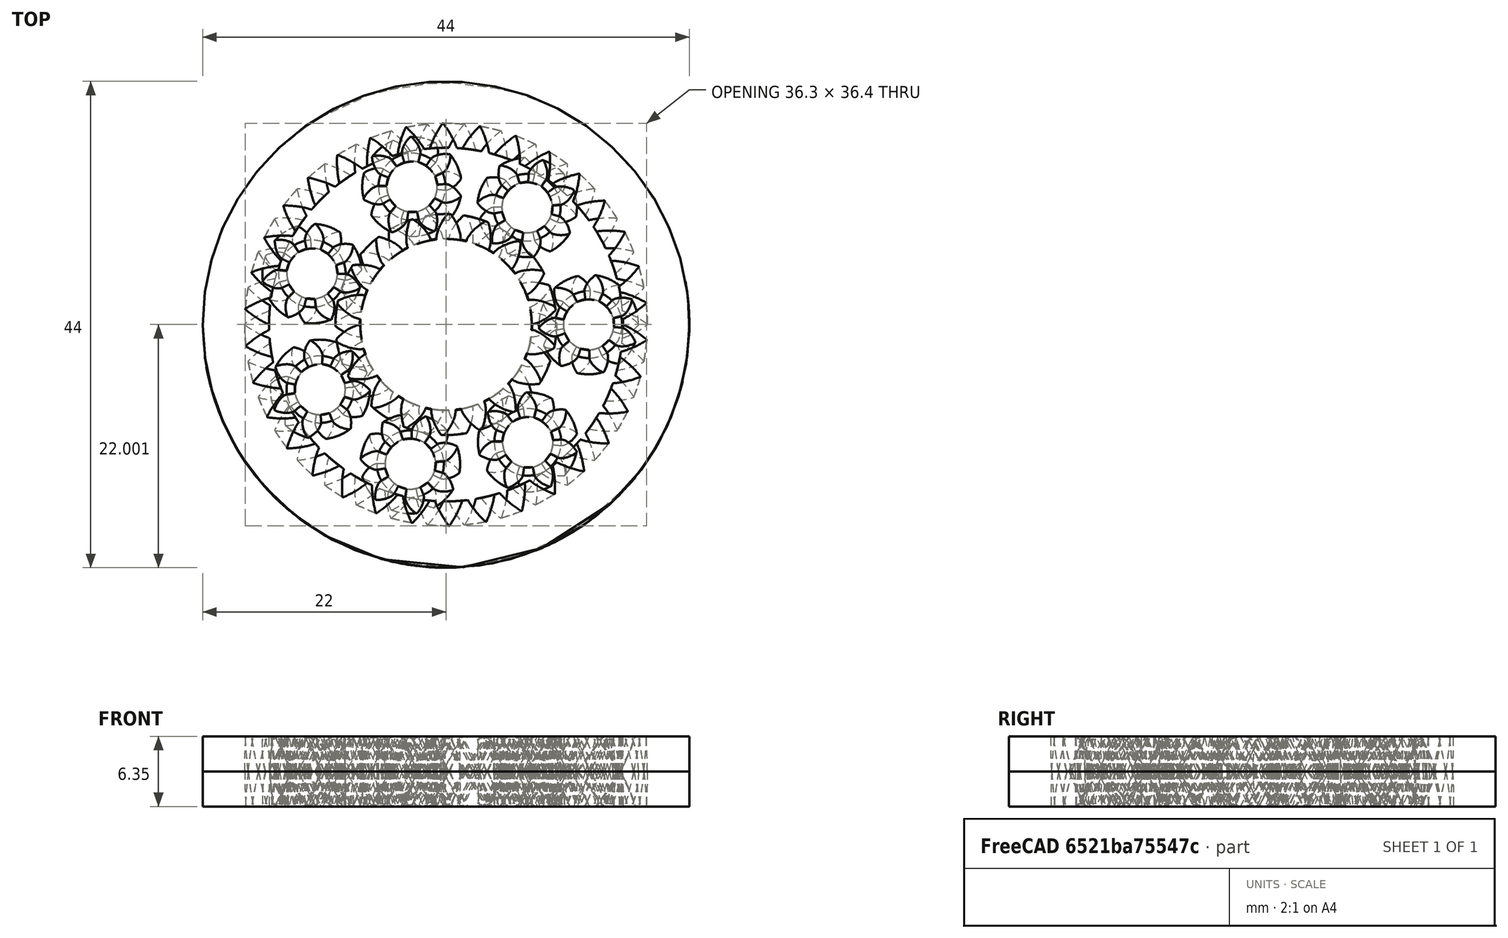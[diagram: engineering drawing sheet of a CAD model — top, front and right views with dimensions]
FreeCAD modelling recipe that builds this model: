
FCSTD DOCUMENT  (FreeCAD 0.20R29410 (Git))
Label: bearing
License: All rights reserved
LicenseURL: http://en.wikipedia.org/wiki/All_rights_reserved
objects: PartDesign::FeatureBase×8, PartDesign::Body×8, Part::FeaturePython×3
note: 19 computed .brp shape members not serialized (recipe doc carries the construction recipe); baked Part::Feature solids carry a one-line shape summary decoded from their .brp

FEATURE [Part::FeaturePython] InternalInvoluteGear  # WARN: FeaturePython — macro-defined, semantics opaque (R4)
  AttacherType = Attacher::AttachEngine3D
  angular_backlash = 0
  backlash = 0
  beta = 30
  clearance = 0.2
  da = 32
  df = 36.4
  double_helix = true
  dw = 34
  head = 0
  head_fillet = 0
  height = 6.35
  module = 1
  numpoints = 6
  outside_diameter = 44
  pressure_angle = 30
  properties_from_tool = false
  reversed_backlash = false
  root_fillet = 0
  shift = 0
  simple = false
  teeth = 34
  thickness = 5
  transverse_pitch = 3.14159
  version = 0.0.4
  expr: angular_backlash = backlash / dw * 360° / pi
  expr: dw = teeth * module
FEATURE [Part::FeaturePython] InvoluteGear  # WARN: FeaturePython — macro-defined, semantics opaque (R4)
  AttacherType = Attacher::AttachEngine3D
  Placement = pos=(12.9,0,0) rot=(0,0,1;0rad)
  angular_backlash = 0
  backlash = 0
  beta = 30
  clearance = 0.2
  da = 9
  df = 4.6
  double_helix = true
  dw = 7
  head = 0
  head_fillet = 0
  height = 6.35
  module = 1
  numpoints = 6
  pressure_angle = 30
  properties_from_tool = false
  reversed_backlash = false
  root_fillet = 0
  shift = 0
  simple = false
  teeth = 7
  transverse_pitch = 3.14159
  undercut = false
  version = 0.0.4
  expr: angular_backlash = backlash / dw * 360° / pi
  expr: dw = teeth * module
FEATURE [Part::FeaturePython] InvoluteGear001  # WARN: FeaturePython — macro-defined, semantics opaque (R4)
  AttacherType = Attacher::AttachEngine3D
  angular_backlash = 0
  backlash = 0
  beta = -30
  clearance = 0.25
  da = 20
  df = 15.5
  double_helix = true
  dw = 18
  head = 0
  head_fillet = 0
  height = 6.35
  module = 1
  numpoints = 6
  pressure_angle = 30
  properties_from_tool = false
  reversed_backlash = false
  root_fillet = 0
  shift = 0
  simple = false
  teeth = 18
  transverse_pitch = 3.14159
  undercut = false
  version = 0.0.4
  expr: angular_backlash = backlash / dw * 360° / pi
  expr: dw = teeth * module
FEATURE [PartDesign::FeatureBase] BaseFeature001
  BaseFeature = -> InvoluteGear
FEATURE [PartDesign::Body] Body001
  BaseFeature = -> InvoluteGear
  Group = -> [BaseFeature001]
  Origin = -> Origin001
  Placement = pos=(12.9,0,0) rot=(0,0,1;0rad)
  Tip = -> BaseFeature001
FEATURE [PartDesign::FeatureBase] BaseFeature002
  BaseFeature = -> InvoluteGear
FEATURE [PartDesign::Body] Body002
  BaseFeature = -> InvoluteGear
  Group = -> [BaseFeature002]
  Origin = -> Origin002
  Placement = pos=(7.33473,10.597,0) rot=(0,0,1;6.10865rad)
  Tip = -> BaseFeature002
FEATURE [PartDesign::FeatureBase] BaseFeature003
  BaseFeature = -> InvoluteGear
FEATURE [PartDesign::Body] Body003
  BaseFeature = -> InvoluteGear
  Group = -> [BaseFeature003]
  Origin = -> Origin003
  Placement = pos=(-3.07413,12.4733,0) rot=(0,0,1;0.174533rad)
  Tip = -> BaseFeature003
FEATURE [PartDesign::FeatureBase] BaseFeature004
  BaseFeature = -> InvoluteGear
FEATURE [PartDesign::Body] Body004
  BaseFeature = -> InvoluteGear
  Group = -> [BaseFeature004]
  Origin = -> Origin004
  Placement = pos=(-12.1091,4.60834,0) rot=(0,0,1;0.087266rad)
  Tip = -> BaseFeature004
FEATURE [PartDesign::FeatureBase] BaseFeature005
  BaseFeature = -> InvoluteGear
FEATURE [PartDesign::Body] Body005
  BaseFeature = -> InvoluteGear
  Group = -> [BaseFeature005]
  Origin = -> Origin005
  Placement = pos=(-11.3879,-5.8684,0) rot=(0,0,-1;5.93412rad)
  Tip = -> BaseFeature005
FEATURE [PartDesign::FeatureBase] BaseFeature006
  BaseFeature = -> InvoluteGear
FEATURE [PartDesign::Body] Body006
  BaseFeature = -> InvoluteGear
  Group = -> [BaseFeature006]
  Origin = -> Origin006
  Placement = pos=(-3.22648,-12.6027,0) rot=(0,0,-1;0.174533rad)
  Tip = -> BaseFeature006
FEATURE [PartDesign::FeatureBase] BaseFeature007
  BaseFeature = -> InvoluteGear
FEATURE [PartDesign::Body] Body007
  BaseFeature = -> InvoluteGear
  Group = -> [BaseFeature007]
  Origin = -> Origin007
  Placement = pos=(7.39437,-10.64,0) rot=(0,0,-1;6.10865rad)
  Tip = -> BaseFeature007
FEATURE [PartDesign::FeatureBase] BaseFeature
  BaseFeature = -> InvoluteGear001
FEATURE [PartDesign::Body] Body
  BaseFeature = -> InvoluteGear001
  Group = -> [BaseFeature]
  Origin = -> Origin
  Tip = -> BaseFeature
